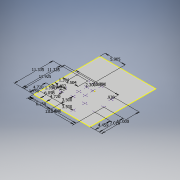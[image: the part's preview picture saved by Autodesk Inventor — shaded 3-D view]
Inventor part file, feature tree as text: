
AUTODESK INVENTOR PART (.ipt)
format: ipt  version: 2017 (Build 210142000, 142)  size: 201,216 bytes
history: native  units: in
note: dims shown in document units (in); Inventor stores cm internally (conversion verified against a paired STEP export)
features: sketch x11, projected_geometry x6, hole x5, extrude x1
ambient origin geometry x8: Origin, YZ Plane, XZ Plane, XY Plane, X Axis, Y Axis, Z Axis, Center Point
bodies: Solid1 (feature_tree)
feature tree (23):
  extrude  "PDU bottom"  Depth=16.45in
  sketch  "Sketch2"  dims[d2=0.065in d3=0.0in d4=6.25in]
  sketch  "Sketch3"  dims[d5=1.75in d7=0.7874in d9=3.5in d10=0.7874in d12=3.5in]
  sketch  "Sketch4"  dims[d22=13.54in d23=4.459in]
  hole  "enable holes"  [1 undecoded]
  hole  "Inteface circuit board holes "  [1 undecoded]
  hole  "snap psu holes"  [1 undecoded]
  sketch  "Sketch10"  dims[d73=0.134in d74=0.2362in d75=0.248in d76=0.0787in d77=90.0deg d78=0.315in d79=0.8108in]
  hole  "thermostat holes"  [1 undecoded]
  sketch  "Sketch12"  dims[d94=0.134in d95=0.2362in d96=0.248in d97=0.0787in d98=90.0deg d99=0.315in d100=0.8108in]
  hole  "Hole11"  [1 undecoded]
  sketch  "Sketch1"  dims[d0=19.37in d1=16.45in]
  projected_geometry  "Projected Loop1"
  sketch  "Sketch6"  dims[d24=7.018in d25=13.54in]
  projected_geometry  "Projected Loop2"
  sketch  "Sketch7"  dims[d33=5.905in d34=1.1811in d36=2.3in d37=0.7874in d39=1.88in]
  projected_geometry  "Projected Loop3"
  sketch  "Sketch9"  dims[d65=11.925in]
  projected_geometry  "Projected Loop5"
  sketch  "Sketch11"  dims[d80=0.134in d81=0.2362in d82=0.248in d83=0.0787in d84=90.0deg d85=0.315in d86=0.8108in]
  projected_geometry  "Projected Loop6"
  sketch  "Sketch13"  dims[d101=12.59in d102=11.0in d103=0.938in d104=0.1339in d105=0.2362in d106=0.248in d107=0.0787in d108=90.0deg d109=0.315in d110=0.8108in d111=11.335in d112=11.335in d113=1.394in d114=4.504in d115=4.72in d116=3.402in d117=1.394in d118=4.72in d119=6.098in d120=2.949in d121=0.1339in d122=0.2362in d123=0.248in d124=0.0787in d125=90.0deg d126=0.315in d127=0.8108in]
  projected_geometry  "Projected Loop7"
note: 5 required parameter values undecoded (feature->parameter linkage not recoverable at this tier; creation-order binding heuristic only, values carry confidence <= 0.55)
